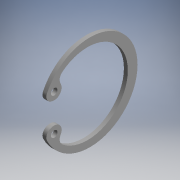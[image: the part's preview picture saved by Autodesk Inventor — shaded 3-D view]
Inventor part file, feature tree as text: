
AUTODESK INVENTOR PART (.ipt)
format: ipt  version: 2017.3 (Build 213256000, 256)  size: 115,200 bytes
history: native  units: mm (DEFAULTED — no unit token found)
features: other x7, extrude x1, sketch x1
ambient origin geometry x8: Origin, YZ Plane, XZ Plane, XY Plane, X Axis, Y Axis, Z Axis, Center Point
bodies: Solid1 (feature_tree)
feature tree (9):
  extrude  "Extrusion1"  TaperAngle=0.0deg  [1 undecoded]
  other  "rr_XY"
  other  "rr_YZ"
  other  "rr_ZX"
  other  "rr_X"
  other  "rr_Y"
  other  "rr_Z"
  other  "rr_Center"
  sketch  "Sketch_3"  dims[d0=1.2mm d1=0.0mm d2=0.0mm]
note: 1 required parameter value undecoded (feature->parameter linkage not recoverable at this tier; creation-order binding heuristic only, values carry confidence <= 0.55)
